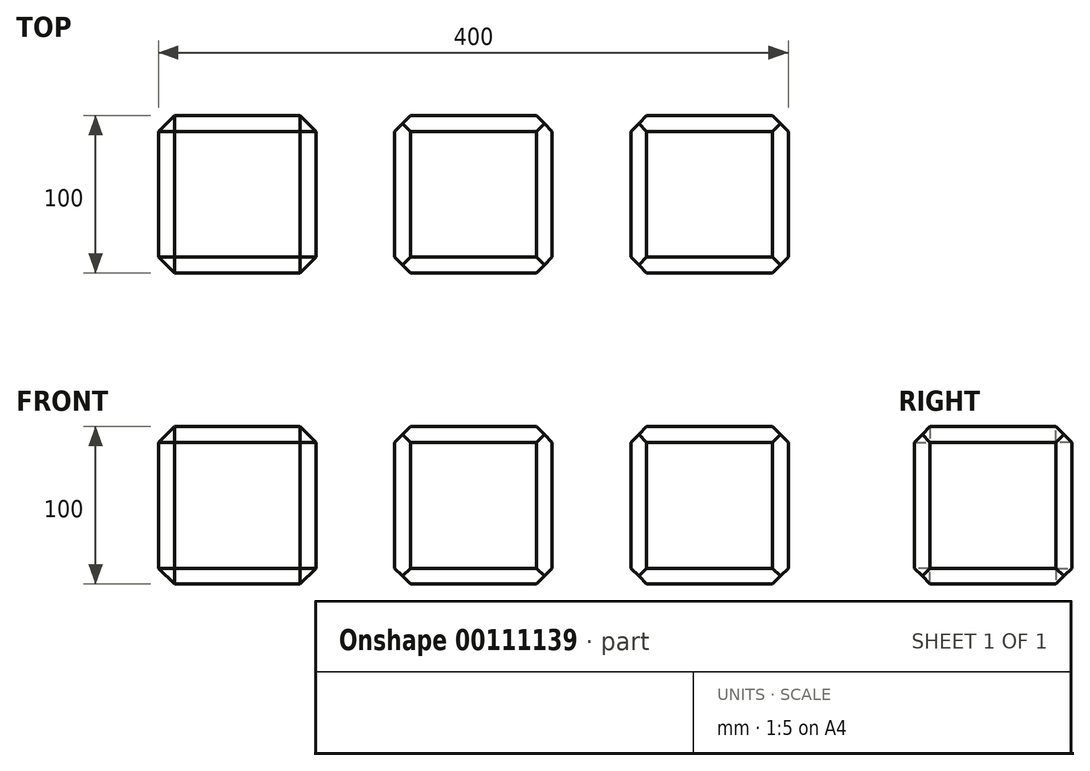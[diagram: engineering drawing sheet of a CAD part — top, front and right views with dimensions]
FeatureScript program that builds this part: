
annotation { "Feature Type Name" : "Feature", "Feature Type Description" : "" }
export const myFeature = defineFeature(function(context is Context, id is Id, definition is map)
    precondition{}
    {
        {
            var Q0;
            Q0=qCreatedBy(makeId("Top.planeOp"),FACE);
            var sketch = newSketch(context, id + "F0", { "sketchPlane" : qUnion([Q0])});
            skLineSegment(sketch, "E0.bottom", {"start": v(-125, 50) * mm, "end": v(-25, 50) * mm});
            skLineSegment(sketch, "E0.top", {"start": v(-125, -50) * mm, "end": v(-25, -50) * mm});
            skLineSegment(sketch, "E0.left", {"start": v(-125, 50) * mm, "end": v(-125, -50) * mm});
            skLineSegment(sketch, "E0.right", {"start": v(-25, 50) * mm, "end": v(-25, -50) * mm});
            skLineSegment(sketch, "E1.bottom", {"start": v(25, 50) * mm, "end": v(125, 50) * mm});
            skLineSegment(sketch, "E1.top", {"start": v(25, -50) * mm, "end": v(125, -50) * mm});
            skLineSegment(sketch, "E1.left", {"start": v(25, 50) * mm, "end": v(25, -50) * mm});
            skLineSegment(sketch, "E1.right", {"start": v(125, 50) * mm, "end": v(125, -50) * mm});
            skLineSegment(sketch, "E2", {"start": v(-25, 0) * mm, "end": v(0, 0) * mm, "construction": true});
            skLineSegment(sketch, "E3", {"start": v(25, 0) * mm, "end": v(0, 0) * mm, "construction": true});
            skLineSegment(sketch, "E4.bottom", {"start": v(175, 50) * mm, "end": v(275, 50) * mm});
            skLineSegment(sketch, "E4.top", {"start": v(175, -50) * mm, "end": v(275, -50) * mm});
            skLineSegment(sketch, "E4.left", {"start": v(175, 50) * mm, "end": v(175, -50) * mm});
            skLineSegment(sketch, "E4.right", {"start": v(275, 50) * mm, "end": v(275, -50) * mm});
            skLineSegment(sketch, "E5", {"start": v(125, 0) * mm, "end": v(150, 0) * mm, "construction": true});
            skLineSegment(sketch, "E6", {"start": v(150, 0) * mm, "end": v(175, 0) * mm, "construction": true});
            skSolve(sketch);
        }
        {
            var Q0;
            Q0 = qSketchRegion(id + "F0", true);
            extrude(context, id + "F1", {"entities" : qUnion([Q0]), "depth" : 100 * mm, "offsetDistance" : 25 * mm});
        }
        {
            var Q0;
            Q0=makeQuery(id+"F1.opExtrude","CAP_FACE",FACE,{"disambiguationData":[OSD([sQuery(id+"F0.wireOp",EDGE,"E0.bottom"),sQuery(id+"F0.wireOp",EDGE,"E0.top"),sQuery(id+"F0.wireOp",EDGE,"E0.left"),sQuery(id+"F0.wireOp",EDGE,"E0.right")])],"isStart":false});
            var Q1;
            Q1=makeQuery(id+"F1.opExtrude","SWEPT_FACE",FACE,{"disambiguationData":[OSD([sQuery(id+"F0.wireOp",EDGE,"E0.right")])]});
            var Q2;
            Q2=makeQuery(id+"F1.opExtrude","SWEPT_FACE",FACE,{"disambiguationData":[OSD([sQuery(id+"F0.wireOp",EDGE,"E0.top")])]});
            var Q3;
            Q3=makeQuery(id+"F1.opExtrude","SWEPT_FACE",FACE,{"disambiguationData":[OSD([sQuery(id+"F0.wireOp",EDGE,"E0.bottom")])]});
            var Q4;
            Q4=makeQuery(id+"F1.opExtrude","SWEPT_FACE",FACE,{"disambiguationData":[OSD([sQuery(id+"F0.wireOp",EDGE,"E0.left")])]});
            var Q5;
            Q5=makeQuery(id+"F1.opExtrude","CAP_FACE",FACE,{"disambiguationData":[OSD([sQuery(id+"F0.wireOp",EDGE,"E0.bottom"),sQuery(id+"F0.wireOp",EDGE,"E0.top"),sQuery(id+"F0.wireOp",EDGE,"E0.left"),sQuery(id+"F0.wireOp",EDGE,"E0.right")])],"isStart":true});
            chamfer(context, id + "F2", {"entities" : qUnion([Q0, Q1, Q2, Q3, Q4, Q5]), "width" : 10 * mm, "tangentPropagation" : true});
        }
        {
            var Q0;
            Q0=makeQuery(id+"F1.opExtrude","CAP_EDGE",EDGE,{"disambiguationData":[OSD([sQuery(id+"F0.wireOp",EDGE,"E1.top")])],"isStart":false});
            var Q1;
            Q1=makeQuery(id+"F1.opExtrude","CAP_EDGE",EDGE,{"disambiguationData":[OSD([sQuery(id+"F0.wireOp",EDGE,"E1.bottom")])],"isStart":false});
            var Q2;
            Q2=makeQuery(id+"F1.opExtrude","CAP_EDGE",EDGE,{"disambiguationData":[OSD([sQuery(id+"F0.wireOp",EDGE,"E1.top")])],"isStart":true});
            var Q3;
            Q3=makeQuery(id+"F1.opExtrude","CAP_EDGE",EDGE,{"disambiguationData":[OSD([sQuery(id+"F0.wireOp",EDGE,"E1.bottom")])],"isStart":true});
            chamfer(context, id + "F3", {"entities" : qUnion([Q0, Q1, Q2, Q3]), "width" : 10 * mm, "tangentPropagation" : true});
        }
        {
            var Q0;
            Q0=makeQuery(id+"F1.opExtrude","CAP_EDGE",EDGE,{"disambiguationData":[OSD([sQuery(id+"F0.wireOp",EDGE,"E1.left")])],"isStart":false});
            var Q1;
            Q1=makeQuery(id+"F1.opExtrude","CAP_EDGE",EDGE,{"disambiguationData":[OSD([sQuery(id+"F0.wireOp",EDGE,"E1.right")])],"isStart":false});
            var Q2;
            Q2=makeQuery(id+"F1.opExtrude","CAP_EDGE",EDGE,{"disambiguationData":[OSD([sQuery(id+"F0.wireOp",EDGE,"E1.right")])],"isStart":true});
            var Q3;
            Q3=makeQuery(id+"F1.opExtrude","CAP_EDGE",EDGE,{"disambiguationData":[OSD([sQuery(id+"F0.wireOp",EDGE,"E1.left")])],"isStart":true});
            chamfer(context, id + "F4", {"entities" : qUnion([Q0, Q1, Q2, Q3]), "width" : 10 * mm, "tangentPropagation" : true});
        }
        {
            var Q0;
            Q0=makeQuery(id+"F1.opExtrude","SWEPT_EDGE",EDGE,{"disambiguationData":[OSD([sQuery(id+"F0.wireOp",EDGE,"E1.bottom"),sQuery(id+"F0.wireOp",EDGE,"E1.left")])]});
            var Q1;
            Q1=makeQuery(id+"F1.opExtrude","SWEPT_EDGE",EDGE,{"disambiguationData":[OSD([sQuery(id+"F0.wireOp",EDGE,"E1.top"),sQuery(id+"F0.wireOp",EDGE,"E1.left")])]});
            var Q2;
            Q2=makeQuery(id+"F1.opExtrude","SWEPT_EDGE",EDGE,{"disambiguationData":[OSD([sQuery(id+"F0.wireOp",EDGE,"E1.top"),sQuery(id+"F0.wireOp",EDGE,"E1.right")])]});
            var Q3;
            Q3=makeQuery(id+"F1.opExtrude","SWEPT_EDGE",EDGE,{"disambiguationData":[OSD([sQuery(id+"F0.wireOp",EDGE,"E1.bottom"),sQuery(id+"F0.wireOp",EDGE,"E1.right")])]});
            chamfer(context, id + "F5", {"entities" : qUnion([Q0, Q1, Q2, Q3]), "width" : 10 * mm, "tangentPropagation" : true});
        }
        {
            var Q0;
            Q0=makeQuery(id+"F1.opExtrude","CAP_FACE",FACE,{"disambiguationData":[OSD([sQuery(id+"F0.wireOp",EDGE,"E4.bottom"),sQuery(id+"F0.wireOp",EDGE,"E4.top"),sQuery(id+"F0.wireOp",EDGE,"E4.left"),sQuery(id+"F0.wireOp",EDGE,"E4.right")])],"isStart":false});
            var Q1;
            Q1=makeQuery(id+"F1.opExtrude","CAP_FACE",FACE,{"disambiguationData":[OSD([sQuery(id+"F0.wireOp",EDGE,"E4.bottom"),sQuery(id+"F0.wireOp",EDGE,"E4.top"),sQuery(id+"F0.wireOp",EDGE,"E4.left"),sQuery(id+"F0.wireOp",EDGE,"E4.right")])],"isStart":true});
            chamfer(context, id + "F6", {"entities" : qUnion([Q0, Q1]), "width" : 10 * mm, "tangentPropagation" : true});
        }
        {
            var Q0;
            Q0=makeQuery(id+"F1.opExtrude","SWEPT_EDGE",EDGE,{"disambiguationData":[OSD([sQuery(id+"F0.wireOp",EDGE,"E4.top"),sQuery(id+"F0.wireOp",EDGE,"E4.right")])]});
            var Q1;
            Q1=makeQuery(id+"F1.opExtrude","SWEPT_EDGE",EDGE,{"disambiguationData":[OSD([sQuery(id+"F0.wireOp",EDGE,"E4.top"),sQuery(id+"F0.wireOp",EDGE,"E4.left")])]});
            var Q2;
            Q2=makeQuery(id+"F1.opExtrude","SWEPT_EDGE",EDGE,{"disambiguationData":[OSD([sQuery(id+"F0.wireOp",EDGE,"E4.bottom"),sQuery(id+"F0.wireOp",EDGE,"E4.left")])]});
            var Q3;
            Q3=makeQuery(id+"F1.opExtrude","SWEPT_EDGE",EDGE,{"disambiguationData":[OSD([sQuery(id+"F0.wireOp",EDGE,"E4.bottom"),sQuery(id+"F0.wireOp",EDGE,"E4.right")])]});
            chamfer(context, id + "F7", {"entities" : qUnion([Q0, Q1, Q2, Q3]), "width" : 10 * mm, "tangentPropagation" : true});
        }
    });
